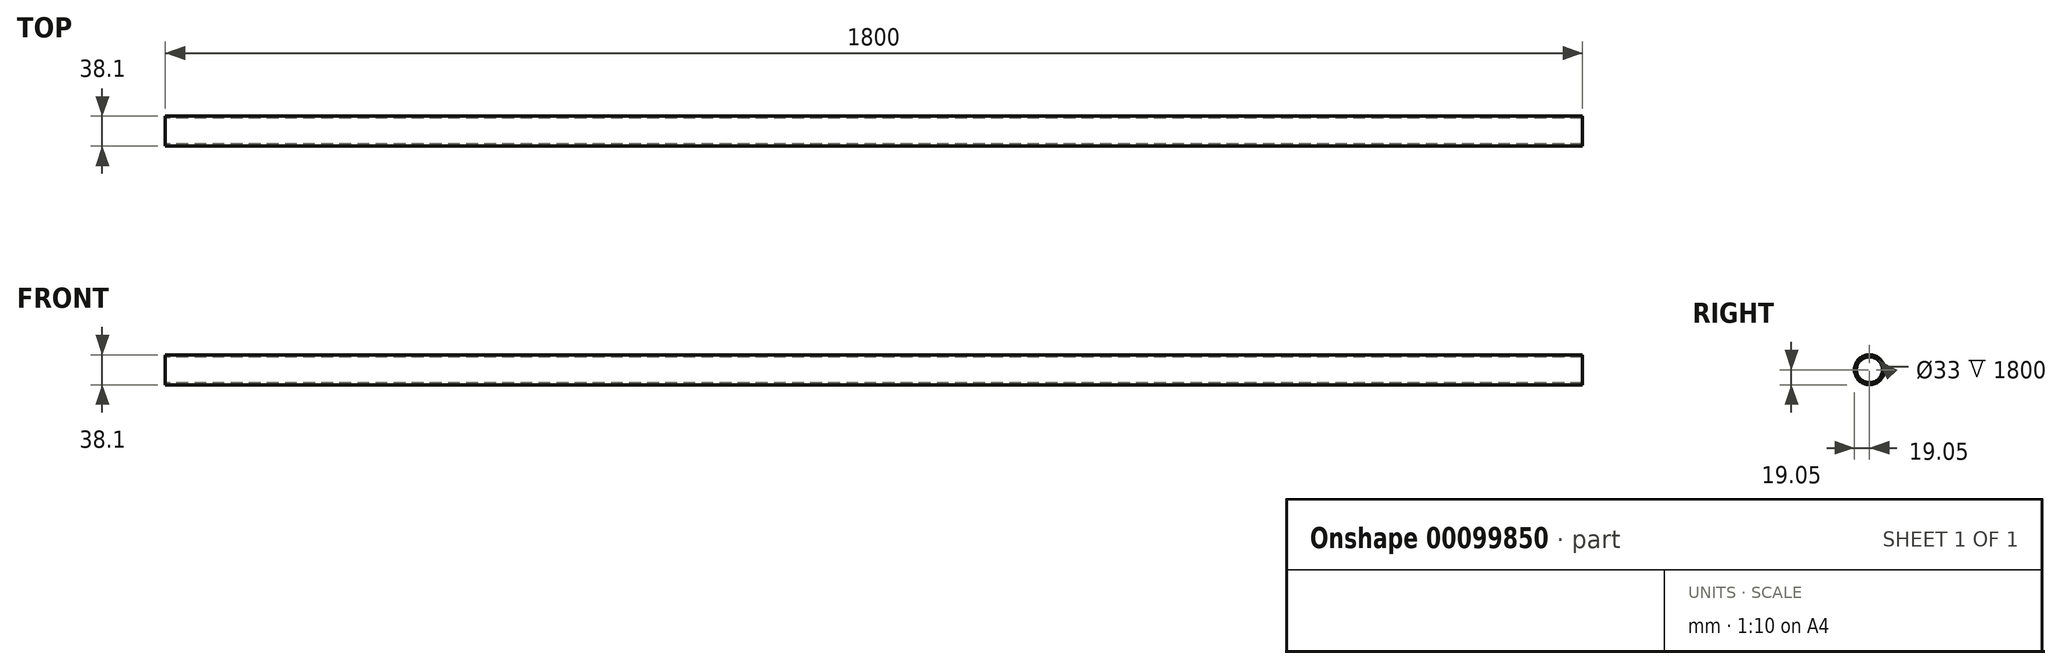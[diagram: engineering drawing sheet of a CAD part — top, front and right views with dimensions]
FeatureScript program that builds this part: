
annotation { "Feature Type Name" : "Feature", "Feature Type Description" : "" }
export const myFeature = defineFeature(function(context is Context, id is Id, definition is map)
    precondition{}
    {
        {
            var Q0;
            Q0=qCreatedBy(makeId("Right.planeOp"),FACE);
            var sketch = newSketch(context, id + "F0", { "sketchPlane" : qUnion([Q0])});
            skCircle(sketch, "E0", {"center": v(0, 0) * mm, "radius": 19.05 * mm});
            skCircle(sketch, "E1", {"center": v(0, 0) * mm, "radius": 16.5 * mm});
            skSolve(sketch);
        }
        {
            var Q0;
            Q0=qSketchRegion(id+"F0",true);
            extrude(context, id + "F1", {"entities" : qUnion([Q0]), "endBound" : BoundingType.SYMMETRIC, "depth" : 1800 * mm});
        }
    });
